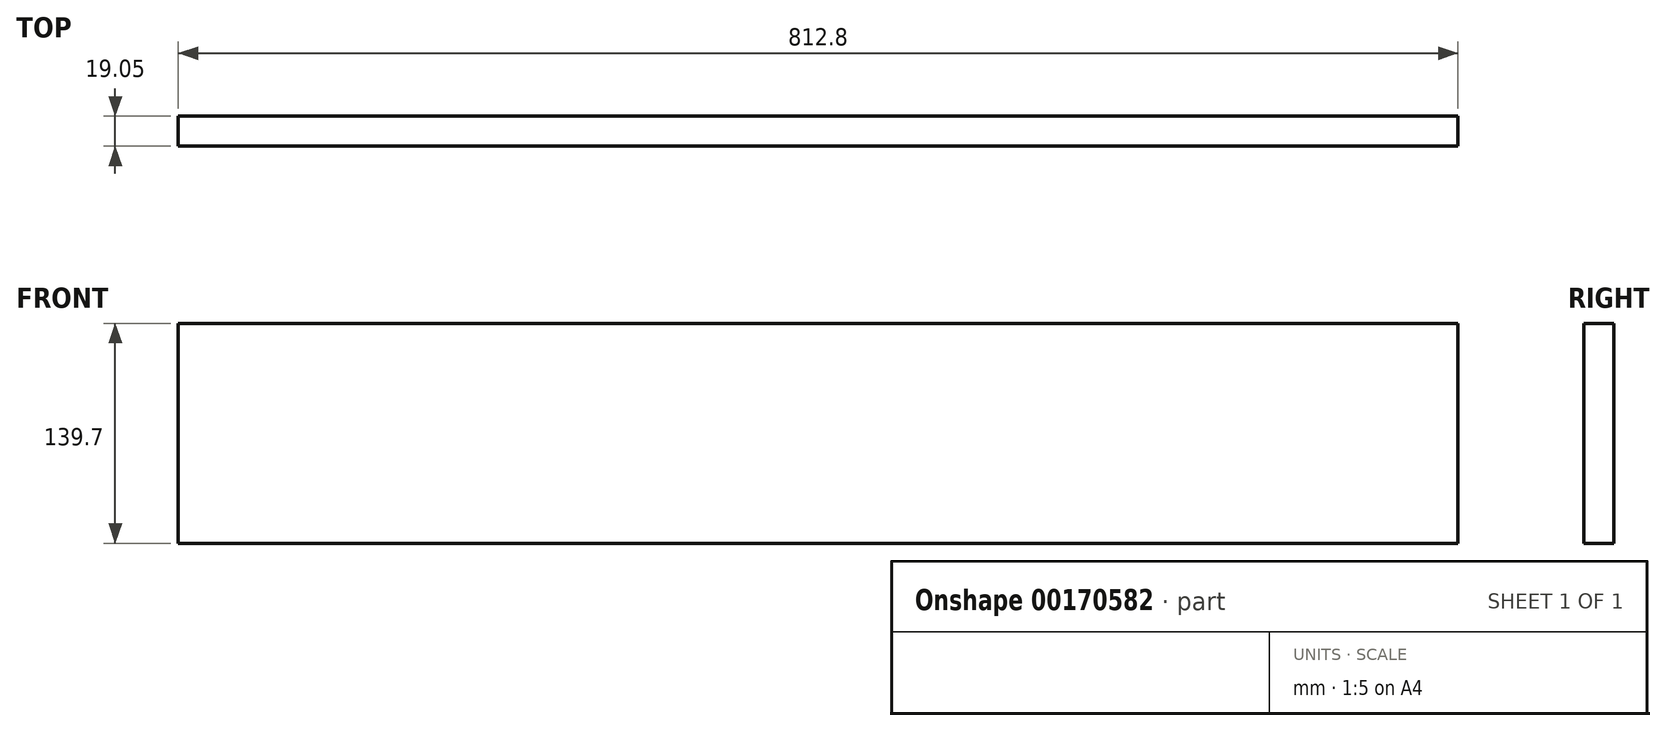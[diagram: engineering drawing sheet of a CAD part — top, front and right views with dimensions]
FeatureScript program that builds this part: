
annotation { "Feature Type Name" : "Feature", "Feature Type Description" : "" }
export const myFeature = defineFeature(function(context is Context, id is Id, definition is map)
    precondition{}
    {
        {
            var Q0;
            Q0=qCreatedBy(makeId("Right.planeOp"),FACE);
            var sketch = newSketch(context, id + "F0", { "sketchPlane" : qUnion([Q0])});
            skLineSegment(sketch, "E0.bottom", {"start": v(0, 69.85) * mm, "end": v(-19.05, 69.85) * mm});
            skLineSegment(sketch, "E0.top", {"start": v(0, -69.85) * mm, "end": v(-19.05, -69.85) * mm});
            skLineSegment(sketch, "E0.left", {"start": v(0, 69.85) * mm, "end": v(0, -69.85) * mm});
            skLineSegment(sketch, "E0.right", {"start": v(-19.05, 69.85) * mm, "end": v(-19.05, -69.85) * mm});
            skSolve(sketch);
        }
        {
            var Q0;
            Q0 = qSketchRegion(id + "F0", true);
            extrude(context, id + "F1", {"entities" : qUnion([Q0]), "endBound" : BoundingType.SYMMETRIC, "depth" : 812.8 * mm});
        }
    });
